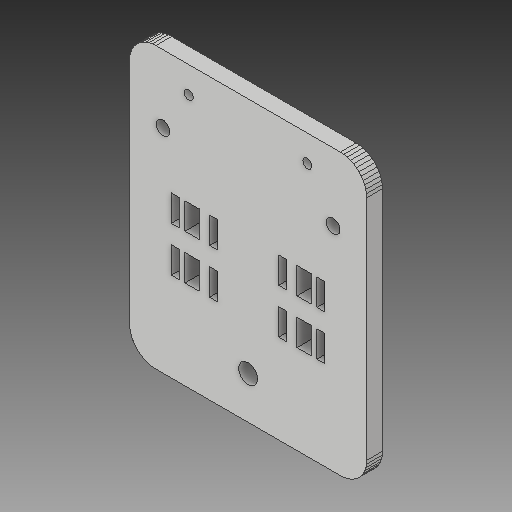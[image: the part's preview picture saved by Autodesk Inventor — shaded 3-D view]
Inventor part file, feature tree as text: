
AUTODESK INVENTOR PART (.ipt)
format: ipt  version: 2018 (Build 220112000, 112)  size: 374,272 bytes
history: native  units: mm
features: sketch x4, hole x3, extrude x1
ambient origin geometry x8: Origin, YZ Plane, XZ Plane, XY Plane, X Axis, Y Axis, Z Axis, Center Point
bodies: Solid1 (feature_tree)
feature tree (8):
  extrude  "Extrusion1"  Depth=6.0mm
  hole  "Hole1"  [1 undecoded]
  hole  "Hole2"  [1 undecoded]
  hole  "Hole3"  [1 undecoded]
  sketch  "Sketch1"  dims[d0=6.0mm d1=0.0mm]
  sketch  "Sketch2"  dims[d2=3.4mm d3=6.0mm d4=4.0mm d5=2.0mm d6=90.0deg d7=8.0mm d8=20.594885mm]
  sketch  "Sketch3"  dims[d9=5.2mm d10=6.0mm d11=4.0mm d12=2.0mm d13=90.0deg d14=8.0mm d15=20.594885mm]
  sketch  "Sketch4"  dims[d16=7.2mm d17=6.0mm d18=4.0mm d19=2.0mm d20=90.0deg d21=8.0mm d22=20.594885mm d23=1.0mm d24=1.0mm]
note: 3 required parameter values undecoded (feature->parameter linkage not recoverable at this tier; creation-order binding heuristic only, values carry confidence <= 0.55)
